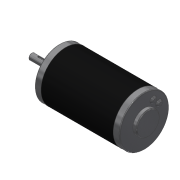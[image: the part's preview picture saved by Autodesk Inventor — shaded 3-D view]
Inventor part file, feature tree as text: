
AUTODESK INVENTOR PART (.ipt)
format: ipt  version: 2016 (Build 200138000, 138)  size: 153,088 bytes
history: native  units: in
note: dims shown in document units (in); Inventor stores cm internally (conversion verified against a paired STEP export)
features: chamfer x1
ambient origin geometry x8: Origin, YZ Plane, XZ Plane, XY Plane, X Axis, Y Axis, Z Axis, Center Point
bodies: Solid1 (feature_tree)
feature tree (1):
  chamfer  "Chamfer3"  [1 undecoded]
note: 1 required parameter value undecoded (feature->parameter linkage not recoverable at this tier; creation-order binding heuristic only, values carry confidence <= 0.55)
